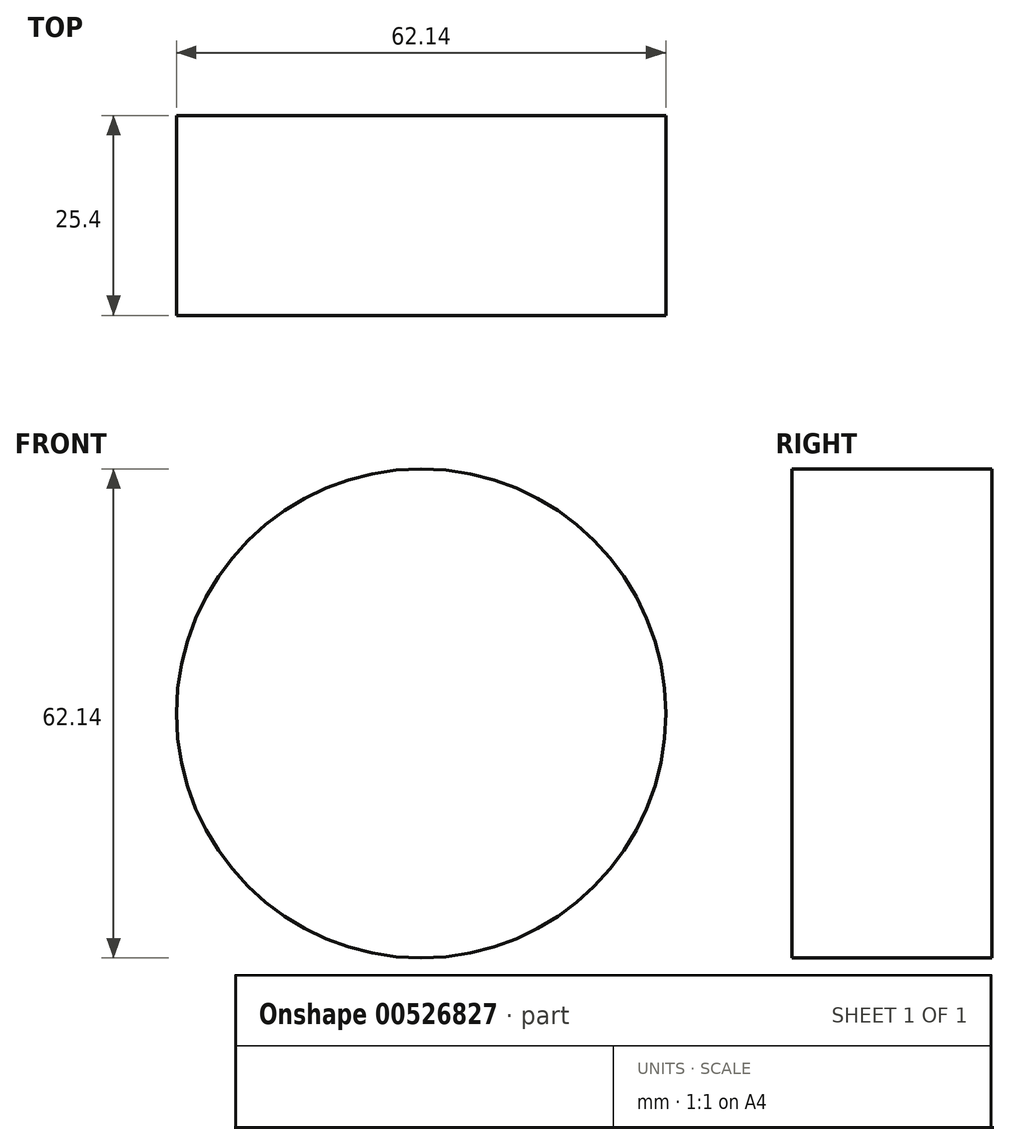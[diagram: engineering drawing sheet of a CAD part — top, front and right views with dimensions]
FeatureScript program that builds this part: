
annotation { "Feature Type Name" : "Feature", "Feature Type Description" : "" }
export const myFeature = defineFeature(function(context is Context, id is Id, definition is map)
    precondition{}
    {
        {
            var Q0;
            Q0=qCreatedBy(makeId("Front.planeOp"),FACE);
            var sketch = newSketch(context, id + "F0", { "sketchPlane" : qUnion([Q0])});
            skCircle(sketch, "E0", {"center": v(0, 0) * mm, "radius": 31.07 * mm});
            skSolve(sketch);
        }
        {
            var Q0;
            Q0=makeQuery(id+"F0.imprint","IMPRINT",FACE,{"disambiguationData":[TD([[makeQuery(id+"F0.imprint","IMPRINT",EDGE,{"derivedFrom":sQuery(id+"F0.wireOp",EDGE,"E0")}),1.0]])]});
            extrude(context, id + "F1", {"entities" : qUnion([Q0]), "depth" : 25.4 * mm, "offsetDistance" : 25.4 * mm});
        }
    });
